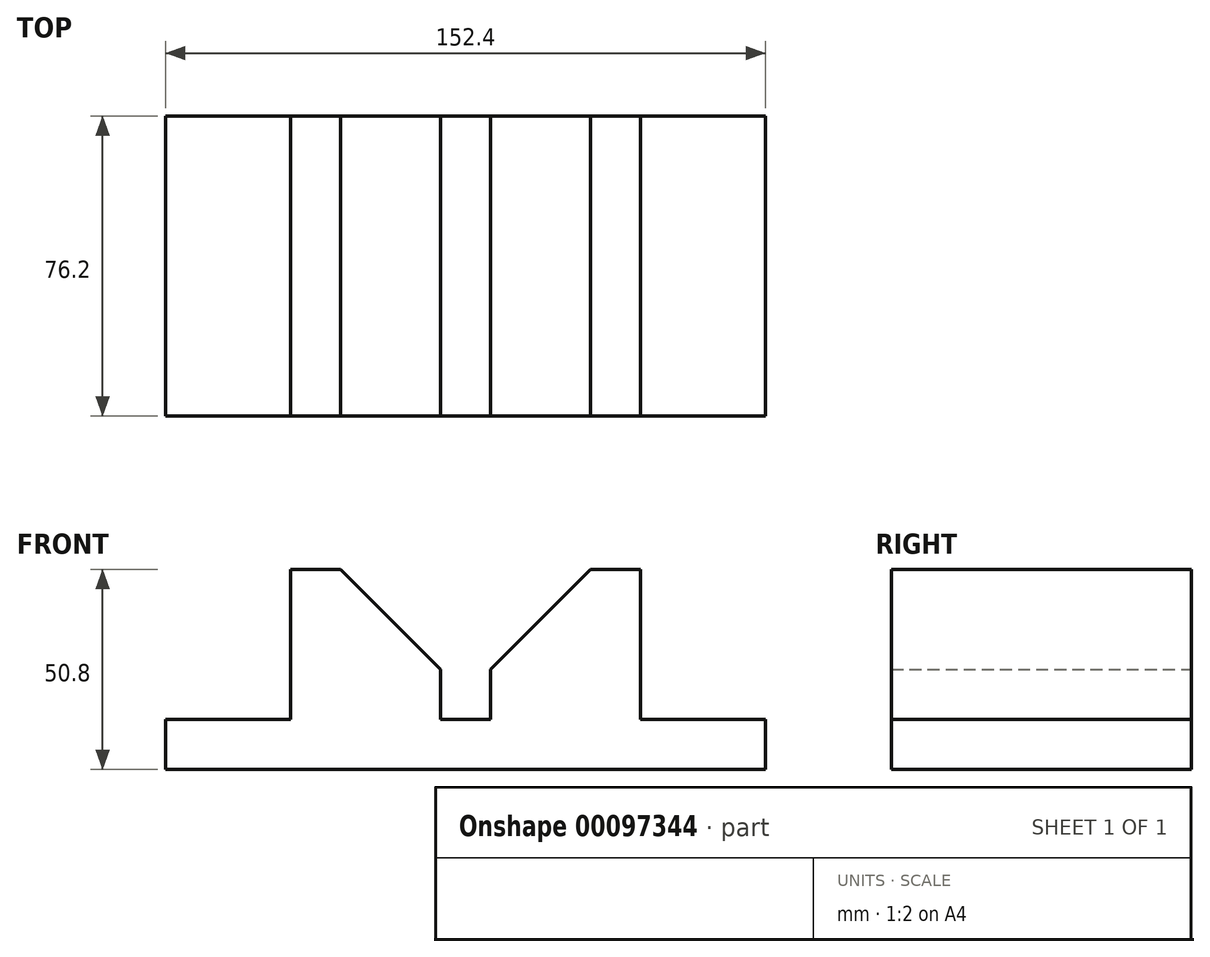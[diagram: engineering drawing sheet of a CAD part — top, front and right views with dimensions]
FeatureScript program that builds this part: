
annotation { "Feature Type Name" : "Feature", "Feature Type Description" : "" }
export const myFeature = defineFeature(function(context is Context, id is Id, definition is map)
    precondition{}
    {
        {
            var Q0;
            Q0=qCreatedBy(makeId("Front.planeOp"),FACE);
            var sketch = newSketch(context, id + "F0", { "sketchPlane" : qUnion([Q0])});
            skLineSegment(sketch, "E0", {"start": v(0, 0) * mm, "end": v(76.2, 0) * mm});
            skLineSegment(sketch, "E1", {"start": v(76.2, 0) * mm, "end": v(76.2, 12.7) * mm});
            skLineSegment(sketch, "E2", {"start": v(76.2, 12.7) * mm, "end": v(44.45, 12.7) * mm});
            skLineSegment(sketch, "E3", {"start": v(44.45, 12.7) * mm, "end": v(44.45, 50.8) * mm});
            skLineSegment(sketch, "E4", {"start": v(44.45, 50.8) * mm, "end": v(31.75, 50.8) * mm});
            skLineSegment(sketch, "E5", {"start": v(31.75, 50.8) * mm, "end": v(6.35, 25.4) * mm});
            skLineSegment(sketch, "E6", {"start": v(6.35, 25.4) * mm, "end": v(6.35, 12.7) * mm});
            skLineSegment(sketch, "E7", {"start": v(6.35, 12.7) * mm, "end": v(0, 12.7) * mm});
            skLineSegment(sketch, "E8", {"start": v(0, 12.7) * mm, "end": v(0, 0) * mm});
            skLineSegment(sketch, "E9.MirrorCS", {"start": v(-6.35, 12.7) * mm, "end": v(0, 12.7) * mm});
            skLineSegment(sketch, "E10.MirrorCS", {"start": v(-44.45, 12.7) * mm, "end": v(-44.45, 50.8) * mm});
            skLineSegment(sketch, "E11.MirrorCS", {"start": v(-44.45, 50.8) * mm, "end": v(-31.75, 50.8) * mm});
            skLineSegment(sketch, "E12.MirrorCS", {"start": v(0, 0) * mm, "end": v(-76.2, 0) * mm});
            skLineSegment(sketch, "E13.MirrorCS", {"start": v(-31.75, 50.8) * mm, "end": v(-6.35, 25.4) * mm});
            skLineSegment(sketch, "E14.MirrorCS", {"start": v(-76.2, 12.7) * mm, "end": v(-44.45, 12.7) * mm});
            skLineSegment(sketch, "E15.MirrorCS", {"start": v(-76.2, 0) * mm, "end": v(-76.2, 12.7) * mm});
            skLineSegment(sketch, "E16.MirrorCS", {"start": v(-6.35, 25.4) * mm, "end": v(-6.35, 12.7) * mm});
            skSolve(sketch);
        }
        {
            var Q0;
            Q0=makeQuery(id+"F0.imprint","IMPRINT",FACE,{"disambiguationData":[TD([[makeQuery(id+"F0.imprint","IMPRINT",EDGE,{"derivedFrom":sQuery(id+"F0.wireOp",EDGE,"E8")}),-1.0]])]});
            var Q1;
            Q1=makeQuery(id+"F0.imprint","IMPRINT",FACE,{"disambiguationData":[TD([[makeQuery(id+"F0.imprint","IMPRINT",EDGE,{"derivedFrom":sQuery(id+"F0.wireOp",EDGE,"E0")}),1.0]])]});
            extrude(context, id + "F1", {"entities" : qUnion([Q0, Q1]), "offsetDistance" : 25.4 * mm, "depth" : 76.2 * mm, "symmetric" : true});
        }
    });
